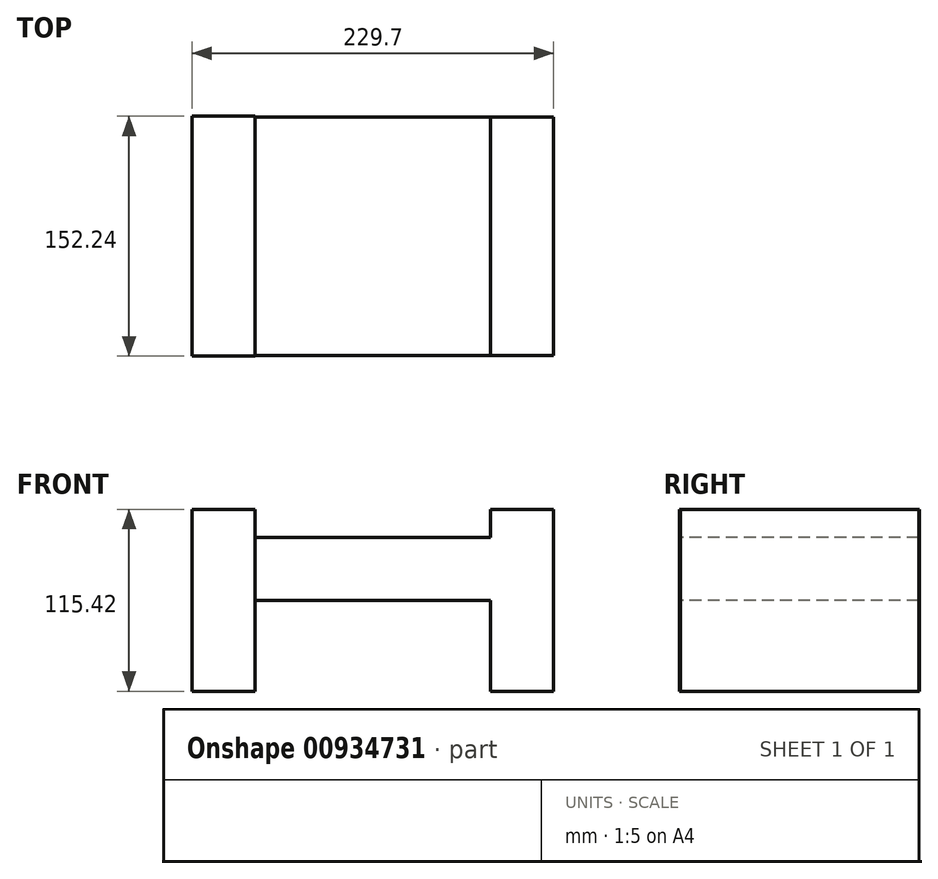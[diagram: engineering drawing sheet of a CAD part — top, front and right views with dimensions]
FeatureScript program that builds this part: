
annotation { "Feature Type Name" : "Feature", "Feature Type Description" : "" }
export const myFeature = defineFeature(function(context is Context, id is Id, definition is map)
    precondition{}
    {
        {
            var Q0;
            Q0=qCreatedBy(makeId("Top.planeOp"),FACE);
            var sketch = newSketch(context, id + "F0", { "sketchPlane" : qUnion([Q0])});
            skLineSegment(sketch, "E0.bottom", {"start": v(-74.85, 75.7) * mm, "end": v(74.85, 75.7) * mm});
            skLineSegment(sketch, "E0.top", {"start": v(-74.85, -75.7) * mm, "end": v(74.85, -75.7) * mm});
            skLineSegment(sketch, "E0.left", {"start": v(-74.85, 75.7) * mm, "end": v(-74.85, -75.7) * mm});
            skLineSegment(sketch, "E0.right", {"start": v(74.85, 75.7) * mm, "end": v(74.85, -75.7) * mm});
            skPoint(sketch, "E0.middle", {"position": v(0, 0) * mm});
            skSolve(sketch);
        }
        {
            var Q0;
            Q0 = qSketchRegion(id + "F0", true);
            extrude(context, id + "F1", {"entities" : qUnion([Q0]), "depth" : 40 * mm, "offsetDistance" : 25.4 * mm});
        }
        {
            var Q0;
            Q0=makeQuery(id+"F1.opExtrude","SWEPT_FACE",FACE,{"disambiguationData":[OSD([sQuery(id+"F0.wireOp",EDGE,"E0.right")])]});
            var sketch = newSketch(context, id + "F2", { "sketchPlane" : qUnion([Q0])});
            skLineSegment(sketch, "E1.bottom", {"start": v(-75.7, 57.7) * mm, "end": v(75.7, 57.7) * mm});
            skLineSegment(sketch, "E1.top", {"start": v(-75.7, -57.7) * mm, "end": v(75.7, -57.7) * mm});
            skLineSegment(sketch, "E1.left", {"start": v(-75.7, 57.7) * mm, "end": v(-75.7, -57.7) * mm});
            skLineSegment(sketch, "E1.right", {"start": v(75.7, 57.7) * mm, "end": v(75.7, -57.7) * mm});
            skPoint(sketch, "E1.middle", {"position": v(0, 0) * mm});
            skSolve(sketch);
        }
        {
            var Q0;
            Q0 = qSketchRegion(id + "F2", true);
            extrude(context, id + "F3", {"entities" : qUnion([Q0]), "operationType" : NewBodyOperationType.ADD, "depth" : 40 * mm, "offsetDistance" : 25.4 * mm});
        }
        {
            var Q0;
            Q0=makeQuery(id+"F1.opExtrude","SWEPT_FACE",FACE,{"disambiguationData":[OSD([sQuery(id+"F0.wireOp",EDGE,"E0.left")])]});
            var sketch = newSketch(context, id + "F4", { "sketchPlane" : qUnion([Q0])});
            skLineSegment(sketch, "E2.bottom", {"start": v(-76.12, 57.7) * mm, "end": v(76.12, 57.7) * mm});
            skLineSegment(sketch, "E2.top", {"start": v(-76.12, -57.7) * mm, "end": v(76.12, -57.7) * mm});
            skLineSegment(sketch, "E2.left", {"start": v(-76.12, 57.7) * mm, "end": v(-76.12, -57.7) * mm});
            skLineSegment(sketch, "E2.right", {"start": v(76.12, 57.7) * mm, "end": v(76.12, -57.7) * mm});
            skPoint(sketch, "E2.middle", {"position": v(0, 0) * mm});
            skSolve(sketch);
        }
        {
            var Q0;
            Q0 = qSketchRegion(id + "F4", true);
            extrude(context, id + "F5", {"entities" : qUnion([Q0]), "operationType" : NewBodyOperationType.ADD, "depth" : 40 * mm, "offsetDistance" : 25.4 * mm});
        }
    });
